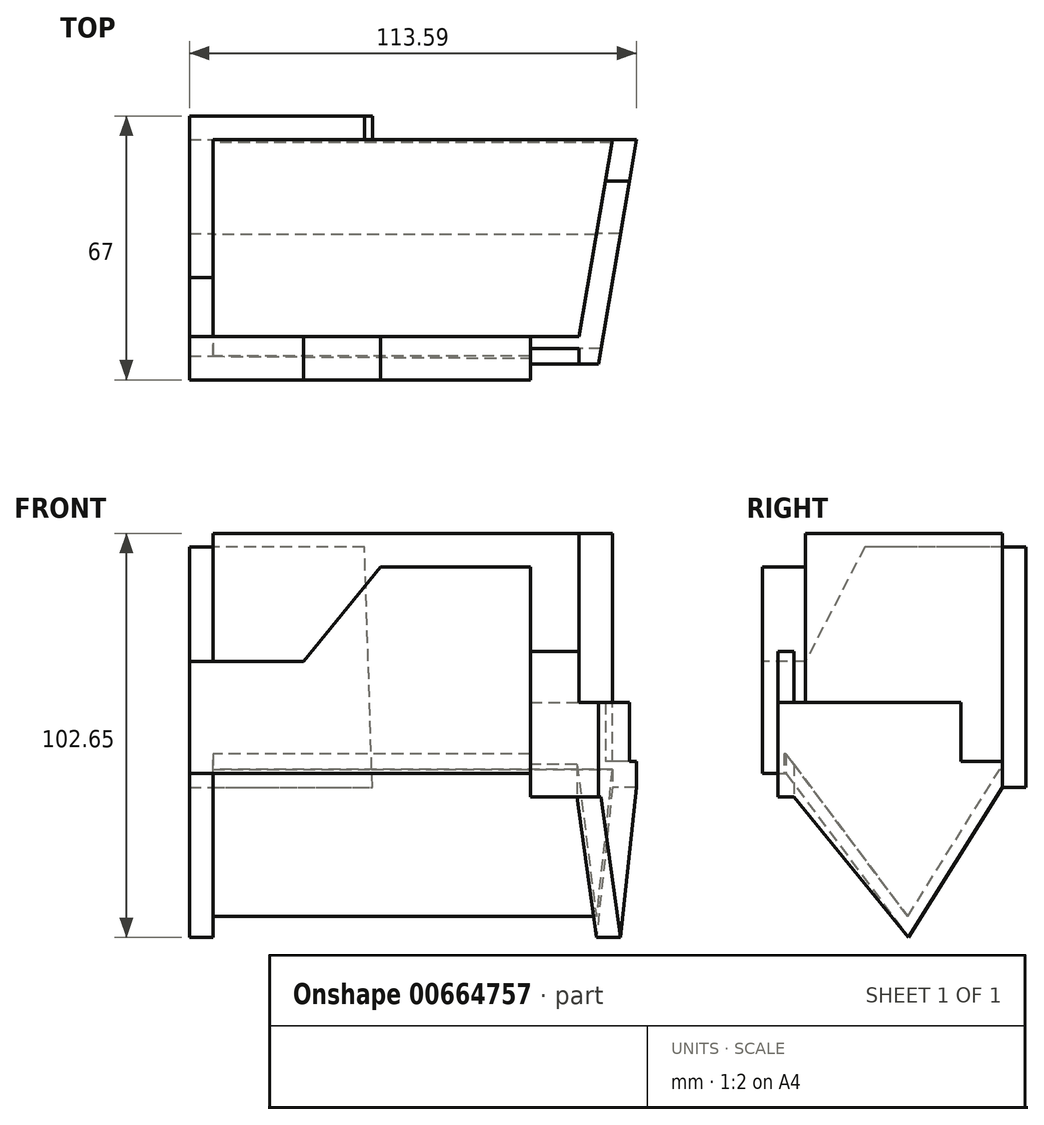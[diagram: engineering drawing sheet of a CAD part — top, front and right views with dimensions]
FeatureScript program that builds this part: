
annotation { "Feature Type Name" : "Feature", "Feature Type Description" : "" }
export const myFeature = defineFeature(function(context is Context, id is Id, definition is map)
    precondition{}
    {
        {
            var Q0;
            Q0=qCreatedBy(makeId("Top.planeOp"),FACE);
            var sketch = newSketch(context, id + "F0", { "sketchPlane" : qUnion([Q0])});
            skLineSegment(sketch, "E0", {"start": v(0, 0) * mm, "end": v(101.5, 0) * mm});
            skLineSegment(sketch, "E1", {"start": v(101.5, 0) * mm, "end": v(93, -50) * mm});
            skLineSegment(sketch, "E2", {"start": v(93, -50) * mm, "end": v(0, -50) * mm});
            skLineSegment(sketch, "E3", {"start": v(0, -50) * mm, "end": v(0, 0) * mm});
            skSolve(sketch);
        }
        {
            var Q0;
            Q0=makeQuery(id+"F0.imprint","IMPRINT",FACE,{"disambiguationData":[TD([[makeQuery(id+"F0.imprint","IMPRINT",EDGE,{"derivedFrom":sQuery(id+"F0.wireOp",EDGE,"E0")}),-1.0]])]});
            extrude(context, id + "F1", {"entities" : qUnion([Q0]), "oppositeDirection" : true, "depth" : 60 * mm, "offsetDistance" : 25 * mm});
        }
        {
            var Q0;
            Q0=makeQuery(id+"F1.opExtrude","SWEPT_FACE",FACE,{"disambiguationData":[OSD([sQuery(id+"F0.wireOp",EDGE,"E0")])]});
            var sketch = newSketch(context, id + "F2", { "sketchPlane" : qUnion([Q0])});
            skLineSegment(sketch, "E4", {"start": v(-38.5, -3.5) * mm, "end": v(6, -3.5) * mm});
            skLineSegment(sketch, "E5", {"start": v(6, -3.5) * mm, "end": v(6, -64.5) * mm});
            skLineSegment(sketch, "E6", {"start": v(6, -64.5) * mm, "end": v(-40.5, -64.5) * mm});
            skLineSegment(sketch, "E7", {"start": v(-40.5, -64.5) * mm, "end": v(-38.5, -3.5) * mm});
            skSolve(sketch);
        }
        {
            var Q0;
            {var subQ5=sQuery(id+"F2.wireOp",EDGE,"E5");Q0=makeQuery(id+"F2.imprint","IMPRINT",FACE,{"disambiguationData":[TD([[makeQuery(id+"F2.imprint","IMPRINT",EDGE,{"derivedFrom":subQ5}),-1.0]])]});}
            var Q1;
            {var subQ0=sQuery(id+"F2.wireOp",EDGE,"E7");var subQ1=sQuery(id+"F2.wireOp",EDGE,"E4");var subQ2=makeQuery(id+"F2.imprint","INTERSECT",VERTEX,{"derivedFrom":[subQ1,subQ0]});Q1=makeQuery(id+"F2.imprint","IMPRINT",FACE,{"disambiguationData":[TD([[makeQuery(id+"F2.imprint","IMPRINT",EDGE,{"disambiguationData":[TD([[subQ2,1.0]])],"derivedFrom":subQ0}),-1.0]])]});}
            extrude(context, id + "F3", {"entities" : qUnion([Q0, Q1]), "operationType" : NewBodyOperationType.ADD, "depth" : 6 * mm, "offsetDistance" : 25 * mm});
        }
        {
            var Q0;
            Q0=makeQuery(id+"F1.opExtrude","SWEPT_FACE",FACE,{"disambiguationData":[OSD([sQuery(id+"F0.wireOp",EDGE,"E3")])]});
            var sketch = newSketch(context, id + "F4", { "sketchPlane" : qUnion([Q0])});
            skLineSegment(sketch, "E8.0.0", {"start": v(0, -64.5) * mm, "end": v(0, -3.5) * mm});
            skLineSegment(sketch, "E8.0.1", {"start": v(0, -3.5) * mm, "end": v(-6, -3.5) * mm});
            skLineSegment(sketch, "E8.0.2", {"start": v(-6, -3.5) * mm, "end": v(-6, -64.5) * mm});
            skLineSegment(sketch, "E8.0.3", {"start": v(-6, -64.5) * mm, "end": v(0, -64.5) * mm});
            skLineSegment(sketch, "E9", {"start": v(0, -3.5) * mm, "end": v(35, -3.5) * mm});
            skLineSegment(sketch, "E10", {"start": v(35, -3.5) * mm, "end": v(50, -32.5) * mm});
            skLineSegment(sketch, "E11", {"start": v(50, -32.5) * mm, "end": v(61, -32.5) * mm});
            skLineSegment(sketch, "E12", {"start": v(61, -32.5) * mm, "end": v(61, -61) * mm});
            skLineSegment(sketch, "E13", {"start": v(61, -61) * mm, "end": v(55, -61) * mm});
            skLineSegment(sketch, "E14", {"start": v(55, -61) * mm, "end": v(23.87, -102.65) * mm});
            skLineSegment(sketch, "E15", {"start": v(23.87, -102.65) * mm, "end": v(0, -64.5) * mm});
            skLineSegment(sketch, "E16", {"start": v(0, 0) * mm, "end": v(0, -64.5) * mm});
            skSolve(sketch);
        }
        {
            var Q0;
            {var subQ4=sQuery(id+"F4.wireOp",EDGE,"E11");Q0=makeQuery(id+"F4.imprint","IMPRINT",FACE,{"disambiguationData":[TD([[makeQuery(id+"F4.imprint","IMPRINT",EDGE,{"derivedFrom":subQ4}),-1.0]])]});}
            var Q1;
            {var subQ3=sQuery(id+"F4.wireOp",EDGE,"PfmvlqWH-es1l-Y8xX-K0BN-ufrnKSGDMQA0");Q1=makeQuery(id+"F4.imprint","IMPRINT",FACE,{"disambiguationData":[TD([[makeQuery(id+"F4.imprint","IMPRINT",EDGE,{"derivedFrom":subQ3}),-1.0]])]});}
            var Q2;
            {var subQ1=sQuery(id+"F4.wireOp",EDGE,"E9");Q2=makeQuery(id+"F4.imprint","IMPRINT",FACE,{"disambiguationData":[TD([[makeQuery(id+"F4.imprint","IMPRINT",EDGE,{"derivedFrom":subQ1}),-1.0]])]});}
            extrude(context, id + "F5", {"entities" : qUnion([Q0, Q1, Q2]), "operationType" : NewBodyOperationType.ADD, "depth" : 6 * mm, "offsetDistance" : 25 * mm});
        }
        {
            var Q0;
            Q0=makeQuery(id+"F1.opExtrude","SWEPT_FACE",FACE,{"disambiguationData":[OSD([sQuery(id+"F0.wireOp",EDGE,"E2")])]});
            var sketch = newSketch(context, id + "F6", { "sketchPlane" : qUnion([Q0])});
            skLineSegment(sketch, "E17.0.0", {"start": v(0, -61) * mm, "end": v(0, -32.5) * mm});
            skLineSegment(sketch, "E17.0.1", {"start": v(0, -32.5) * mm, "end": v(-6, -32.5) * mm});
            skLineSegment(sketch, "E17.0.2", {"start": v(-6, -32.5) * mm, "end": v(-6, -61) * mm});
            skLineSegment(sketch, "E17.0.3", {"start": v(-6, -61) * mm, "end": v(0, -61) * mm});
            skLineSegment(sketch, "E18", {"start": v(0, -61) * mm, "end": v(80.62, -61) * mm});
            skLineSegment(sketch, "E19", {"start": v(80.62, -61) * mm, "end": v(80.62, -8.5) * mm});
            skLineSegment(sketch, "E20", {"start": v(80.62, -8.5) * mm, "end": v(42.62, -8.5) * mm});
            skLineSegment(sketch, "E21", {"start": v(42.62, -8.5) * mm, "end": v(23, -32.5) * mm});
            skLineSegment(sketch, "E22", {"start": v(23, -32.5) * mm, "end": v(0, -32.5) * mm});
            skSolve(sketch);
        }
        {
            var Q0;
            {var subQ0=sQuery(id+"F6.wireOp",EDGE,"E20");Q0=makeQuery(id+"F6.imprint","IMPRINT",FACE,{"disambiguationData":[TD([[makeQuery(id+"F6.imprint","IMPRINT",EDGE,{"derivedFrom":subQ0}),1.0]])]});}
            var Q1;
            {var subQ3=sQuery(id+"F6.wireOp",EDGE,"E18");Q1=makeQuery(id+"F6.imprint","IMPRINT",FACE,{"disambiguationData":[TD([[makeQuery(id+"F6.imprint","IMPRINT",EDGE,{"derivedFrom":subQ3}),1.0]])]});}
            var Q2;
            Q2=makeQuery(id+"F5.opExtrude","SWEPT_FACE",FACE,{"disambiguationData":[OSD([sQuery(id+"F4.wireOp",EDGE,"E12")])]});
            extrude(context, id + "F7", {"entities" : qUnion([Q0, Q1]), "operationType" : NewBodyOperationType.ADD, "endBound" : BoundingType.UP_TO_SURFACE, "depth" : 25 * mm, "endBoundEntityFace" : qUnion([Q2]), "offsetDistance" : 25 * mm});
        }
        {
            var Q0;
            Q0=makeQuery(id+"F7.boolean.opBoolean","MERGE",FACE,{"derivedFrom":[makeQuery(id+"F5.opExtrude","SWEPT_FACE",FACE,{"disambiguationData":[OSD([sQuery(id+"F4.wireOp",EDGE,"E13")])]}),makeQuery(id+"F7.opExtrude","SWEPT_FACE",FACE,{"disambiguationData":[OSD([sQuery(id+"F6.wireOp",EDGE,"E18")])]})]});
            var sketch = newSketch(context, id + "F8", { "sketchPlane" : qUnion([Q0])});
            skLineSegment(sketch, "E23", {"start": v(0, 55) * mm, "end": v(80.62, 55.5) * mm});
            skLineSegment(sketch, "E24", {"start": v(80.62, 55.5) * mm, "end": v(80.62, 50) * mm});
            skLineSegment(sketch, "E25", {"start": v(80.62, 50) * mm, "end": v(0, 50) * mm});
            skLineSegment(sketch, "E26", {"start": v(0, 50) * mm, "end": v(0, 55) * mm});
            skSolve(sketch);
        }
        {
            var Q0;
            Q0=makeQuery(id+"F8.imprint","IMPRINT",FACE,{"disambiguationData":[TD([[makeQuery(id+"F8.imprint","IMPRINT",EDGE,{"derivedFrom":sQuery(id+"F8.wireOp",EDGE,"E23")}),-1.0]])]});
            extrude(context, id + "F9", {"entities" : qUnion([Q0]), "operationType" : NewBodyOperationType.REMOVE, "oppositeDirection" : true, "depth" : 5 * mm, "offsetDistance" : 25 * mm});
        }
        {
            var Q0;
            Q0=makeQuery(id+"F9.boolean.opBoolean","MERGE",FACE,{"derivedFrom":[makeQuery(id+"F5.opExtrude","CAP_FACE",FACE,{"disambiguationData":[OSD([sQuery(id+"F4.wireOp",EDGE,"E9"),sQuery(id+"F4.wireOp",EDGE,"E10"),sQuery(id+"F4.wireOp",EDGE,"E11"),sQuery(id+"F4.wireOp",EDGE,"E12"),sQuery(id+"F4.wireOp",EDGE,"E13"),sQuery(id+"F4.wireOp",EDGE,"E14"),sQuery(id+"F4.wireOp",EDGE,"E15"),sQuery(id+"F4.wireOp",EDGE,"E16")])],"isStart":true}),makeQuery(id+"F9.opExtrude","SWEPT_FACE",FACE,{"disambiguationData":[OSD([sQuery(id+"F8.wireOp",EDGE,"E26")])]})]});
            var sketch = newSketch(context, id + "F10", { "sketchPlane" : qUnion([Q0])});
            skLineSegment(sketch, "E27.0", {"start": v(-24.09, -97.34) * mm, "end": v(-2.55, -62.91) * mm});
            skLineSegment(sketch, "E27.1", {"start": v(-52.6, -59.2) * mm, "end": v(-24.09, -97.34) * mm});
            skLineSegment(sketch, "E28", {"start": v(-2.55, -62.91) * mm, "end": v(-0.72, -60) * mm});
            skLineSegment(sketch, "E29", {"start": v(-52.6, -59.2) * mm, "end": v(-55, -55.99) * mm});
            skLineSegment(sketch, "E30", {"start": v(-55, -55.99) * mm, "end": v(-50, -55.99) * mm});
            skLineSegment(sketch, "E31", {"start": v(-50, -55.99) * mm, "end": v(-50, -60) * mm});
            skLineSegment(sketch, "E32", {"start": v(-50, -60) * mm, "end": v(-0.72, -60) * mm});
            skSolve(sketch);
        }
        {
            var Q0;
            Q0=makeQuery(id+"F10.imprint","IMPRINT",FACE,{"disambiguationData":[TD([[makeQuery(id+"F10.imprint","IMPRINT",EDGE,{"derivedFrom":sQuery(id+"F10.wireOp",EDGE,"E27.0")}),1.0]])]});
            var Q1;
            Q1=makeQuery(id+"F1.opExtrude","SWEPT_FACE",FACE,{"disambiguationData":[OSD([sQuery(id+"F0.wireOp",EDGE,"E1")])]});
            extrude(context, id + "F11", {"entities" : qUnion([Q0]), "operationType" : NewBodyOperationType.ADD, "endBound" : BoundingType.UP_TO_SURFACE, "depth" : 25 * mm, "endBoundEntityFace" : qUnion([Q1]), "offsetDistance" : 25 * mm});
        }
        {
            var Q0;
            Q0=makeQuery(id+"F9.boolean.opBoolean","MERGE",FACE,{"derivedFrom":[makeQuery(id+"F1.opExtrude","SWEPT_FACE",FACE,{"disambiguationData":[OSD([sQuery(id+"F0.wireOp",EDGE,"E2")])]}),makeQuery(id+"F9.opExtrude","SWEPT_FACE",FACE,{"disambiguationData":[OSD([sQuery(id+"F8.wireOp",EDGE,"E25")])]})]});
            var sketch = newSketch(context, id + "F12", { "sketchPlane" : qUnion([Q0])});
            skLineSegment(sketch, "E33", {"start": v(80.62, -30) * mm, "end": v(93, -30) * mm});
            skLineSegment(sketch, "E34", {"start": v(80.62, -30) * mm, "end": v(80.62, -67) * mm});
            skLineSegment(sketch, "E35", {"start": v(80.62, -67) * mm, "end": v(99.12, -67) * mm});
            skLineSegment(sketch, "E36", {"start": v(99.12, -67) * mm, "end": v(99.12, -30) * mm});
            skLineSegment(sketch, "E37", {"start": v(99.12, -30) * mm, "end": v(93, -30) * mm});
            skLineSegment(sketch, "E38", {"start": v(93, -30) * mm, "end": v(93, -43) * mm});
            skLineSegment(sketch, "E39", {"start": v(99.12, -43) * mm, "end": v(93, -43) * mm});
            skSolve(sketch);
        }
        {
            var Q0;
            {var subQ2=sQuery(id+"F12.wireOp",EDGE,"E35");Q0=makeQuery(id+"F12.imprint","IMPRINT",FACE,{"disambiguationData":[TD([[makeQuery(id+"F12.imprint","IMPRINT",EDGE,{"derivedFrom":subQ2}),1.0]])]});}
            var Q1;
            {var subQ1=sQuery(id+"F12.wireOp",EDGE,"E33");Q1=makeQuery(id+"F12.imprint","IMPRINT",FACE,{"disambiguationData":[TD([[makeQuery(id+"F12.imprint","IMPRINT",EDGE,{"derivedFrom":subQ1}),-1.0]])]});}
            extrude(context, id + "F13", {"entities" : qUnion([Q0, Q1]), "operationType" : NewBodyOperationType.ADD, "depth" : 7 * mm, "offsetDistance" : 25 * mm, "hasSecondDirection" : true, "secondDirectionOppositeDirection" : false, "secondDirectionDepth" : 3 * mm});
        }
        {
            var Q0;
            Q0=makeQuery(id+"F5.boolean.opBoolean","MERGE",FACE,{"derivedFrom":[makeQuery(id+"F3.opExtrude","SWEPT_FACE",FACE,{"disambiguationData":[OSD([sQuery(id+"F2.wireOp",EDGE,"E5")])]}),makeQuery(id+"F5.opExtrude","CAP_FACE",FACE,{"disambiguationData":[OSD([sQuery(id+"F4.wireOp",EDGE,"E9"),sQuery(id+"F4.wireOp",EDGE,"E10"),sQuery(id+"F4.wireOp",EDGE,"E11"),sQuery(id+"F4.wireOp",EDGE,"E12"),sQuery(id+"F4.wireOp",EDGE,"E13"),sQuery(id+"F4.wireOp",EDGE,"E14"),sQuery(id+"F4.wireOp",EDGE,"E15"),sQuery(id+"F4.wireOp",EDGE,"E16")])],"isStart":false})]});
            var sketch = newSketch(context, id + "F14", { "sketchPlane" : qUnion([Q0])});
            skLineSegment(sketch, "E40", {"start": v(23.87, -102.65) * mm, "end": v(0, -64.5) * mm});
            skLineSegment(sketch, "E41", {"start": v(0, -64.5) * mm, "end": v(0, -61) * mm, "construction": true});
            skLineSegment(sketch, "E42", {"start": v(0, -61) * mm, "end": v(0, -64.5) * mm});
            skLineSegment(sketch, "E43", {"start": v(10.5, -58) * mm, "end": v(10.5, -43) * mm});
            skLineSegment(sketch, "E44", {"start": v(10.5, -43) * mm, "end": v(57.5, -43) * mm});
            skLineSegment(sketch, "E45.0.2", {"start": v(57, -43) * mm, "end": v(57, -67) * mm});
            skLineSegment(sketch, "E45.0.3", {"start": v(57, -67) * mm, "end": v(53, -67) * mm});
            skLineSegment(sketch, "E46", {"start": v(53, -67) * mm, "end": v(23.87, -102.65) * mm});
            skLineSegment(sketch, "E47", {"start": v(0, -64.5) * mm, "end": v(0, -58) * mm});
            skLineSegment(sketch, "E48", {"start": v(10.5, -58) * mm, "end": v(0, -58) * mm});
            skSolve(sketch);
        }
        {
            var Q0;
            {var subQ6=sQuery(id+"F14.wireOp",EDGE,"E40");Q0=makeQuery(id+"F14.imprint","IMPRINT",FACE,{"disambiguationData":[TD([[makeQuery(id+"F14.imprint","IMPRINT",EDGE,{"derivedFrom":subQ6}),-1.0]])]});}
            var Q1;
            {var subQ1=sQuery(id+"F14.wireOp",EDGE,"E45.0.3");Q1=makeQuery(id+"F14.imprint","IMPRINT",FACE,{"disambiguationData":[TD([[makeQuery(id+"F14.imprint","IMPRINT",EDGE,{"derivedFrom":subQ1}),-1.0]])]});}
            var Q2;
            {var subQ0=sQuery(id+"F0.wireOp",EDGE,"E1");Q2=makeQuery(id+"F11.boolean.opBoolean","MERGE",FACE,{"derivedFrom":[makeQuery(id+"F1.opExtrude","SWEPT_FACE",FACE,{"disambiguationData":[OSD([subQ0])]}),makeQuery(id+"F11.opExtrude","CAP_FACE",FACE,{"disambiguationData":[OSD([subQ0])],"isStart":false})]});}
            extrude(context, id + "F15", {"entities" : qUnion([Q0, Q1]), "oppositeDirection" : true, "depth" : 126.9 * mm, "offsetDistance" : 25 * mm, "hasSecondDirection" : true, "secondDirectionBound" : SecondDirectionBoundingType.UP_TO_SURFACE, "secondDirectionOppositeDirection" : true, "secondDirectionDepth" : 98.8 * mm, "secondDirectionBoundEntityFace" : qUnion([Q2])});
        }
        {
            var Q0;
            {var subQ0=sQuery(id+"F0.wireOp",EDGE,"E1");Q0=makeQuery(id+"F11.boolean.opBoolean","MERGE",FACE,{"derivedFrom":[makeQuery(id+"F1.opExtrude","SWEPT_FACE",FACE,{"disambiguationData":[OSD([subQ0])]}),makeQuery(id+"F11.opExtrude","CAP_FACE",FACE,{"disambiguationData":[OSD([subQ0])],"isStart":false})]});}
            var sketch = newSketch(context, id + "F16", { "sketchPlane" : qUnion([Q0])});
            skLineSegment(sketch, "E49.bottom", {"start": v(75.24, 30.64) * mm, "end": v(-98.22, 30.64) * mm});
            skLineSegment(sketch, "E49.top", {"start": v(75.24, -109.36) * mm, "end": v(-98.22, -109.36) * mm});
            skLineSegment(sketch, "E49.left", {"start": v(75.24, 30.64) * mm, "end": v(75.24, -109.36) * mm});
            skLineSegment(sketch, "E49.right", {"start": v(-98.22, 30.64) * mm, "end": v(-98.22, -109.36) * mm});
            skSolve(sketch);
        }
        {
            var Q0;
            Q0 = qSketchRegion(id + "F16", true);
            extrude(context, id + "F17", {"entities" : qUnion([Q0]), "operationType" : NewBodyOperationType.REMOVE, "depth" : 54.4 * mm, "offsetDistance" : 25 * mm, "hasSecondDirection" : true, "secondDirectionOppositeDirection" : false, "secondDirectionDepth" : 6 * mm});
        }
        {
            var Q0;
            Q0=makeQuery(id+"F11.opExtrude","SWEPT_FACE",FACE,{"disambiguationData":[OSD([sQuery(id+"F8.wireOp",EDGE,"E26")])]});
            var sketch = newSketch(context, id + "F18", { "sketchPlane" : qUnion([Q0])});
            skLineSegment(sketch, "E50", {"start": v(80.62, -50) * mm, "end": v(80.62, -53) * mm});
            skLineSegment(sketch, "E51", {"start": v(80.62, -53) * mm, "end": v(92.49, -53) * mm});
            skLineSegment(sketch, "E52", {"start": v(92.49, -53) * mm, "end": v(93, -50) * mm});
            skLineSegment(sketch, "E53", {"start": v(93, -50) * mm, "end": v(80.62, -50) * mm});
            skSolve(sketch);
        }
        {
            var Q0;
            Q0=makeQuery(id+"F18.imprint","IMPRINT",FACE,{"disambiguationData":[TD([[makeQuery(id+"F18.imprint","IMPRINT",EDGE,{"derivedFrom":sQuery(id+"F18.wireOp",EDGE,"E50")}),-1.0]])]});
            var Q1;
            Q1=makeQuery(id+"F15.opExtrude","SWEPT_FACE",FACE,{"disambiguationData":[OSD([sQuery(id+"F14.wireOp",EDGE,"E44")])]});
            extrude(context, id + "F19", {"entities" : qUnion([Q0]), "operationType" : NewBodyOperationType.ADD, "endBound" : BoundingType.UP_TO_SURFACE, "depth" : 25 * mm, "endBoundEntityFace" : qUnion([Q1]), "offsetDistance" : 25 * mm});
        }
    });
